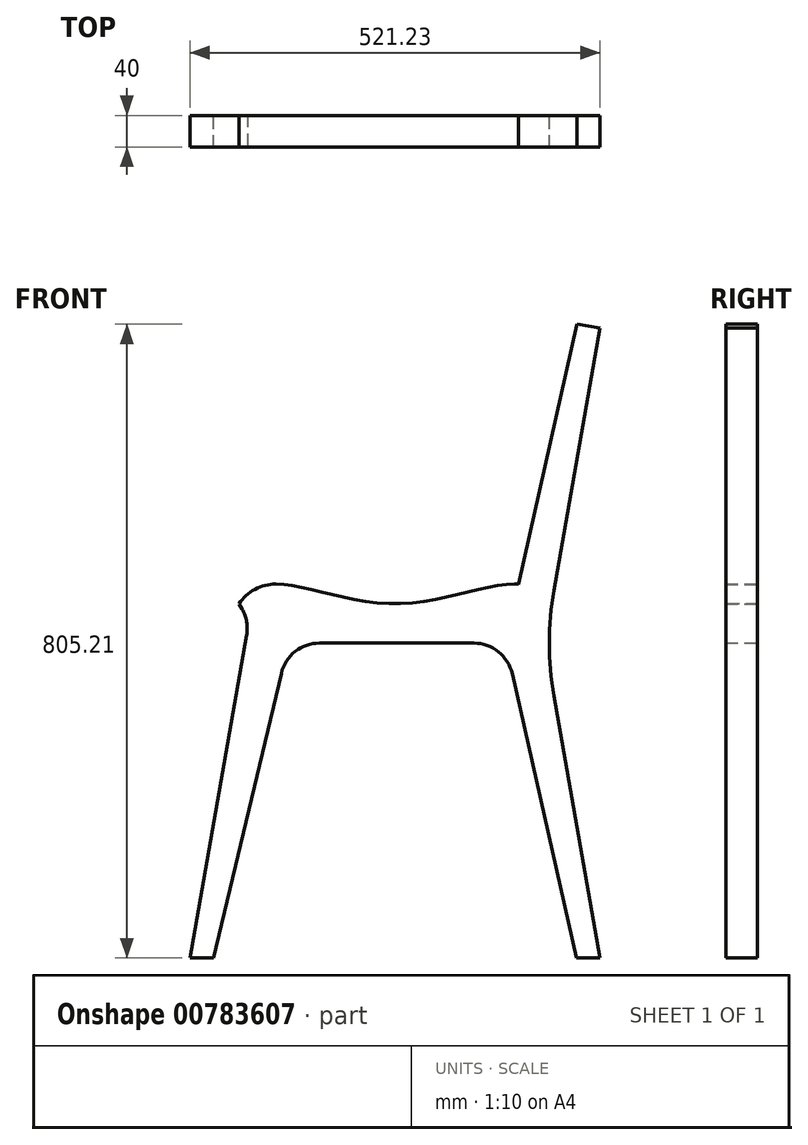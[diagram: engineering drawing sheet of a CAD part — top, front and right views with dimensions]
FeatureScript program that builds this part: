
annotation { "Feature Type Name" : "Feature", "Feature Type Description" : "" }
export const myFeature = defineFeature(function(context is Context, id is Id, definition is map)
    precondition{}
    {
        {
            var Q0;
            Q0=qCreatedBy(makeId("Front.planeOp"),FACE);
            var sketch = newSketch(context, id + "F0", { "sketchPlane" : qUnion([Q0])});
            skLineSegment(sketch, "E0.bottom", {"start": v(-200, 0) * mm, "end": v(200, 0) * mm, "construction": true});
            skLineSegment(sketch, "E0.top", {"start": v(-200, 350) * mm, "end": v(200, 350) * mm, "construction": true});
            skLineSegment(sketch, "E0.left", {"start": v(-200, 0) * mm, "end": v(-200, 350) * mm, "construction": true});
            skLineSegment(sketch, "E0.right", {"start": v(200, 0) * mm, "end": v(200, 350) * mm, "construction": true});
            skLineSegment(sketch, "E1", {"start": v(-200, 0) * mm, "end": v(-200, -450) * mm, "construction": true});
            skLineSegment(sketch, "E2", {"start": v(-200, -450) * mm, "end": v(200, -450) * mm, "construction": true});
            skLineSegment(sketch, "E3", {"start": v(200, -450) * mm, "end": v(200, 0) * mm, "construction": true});
            skLineSegment(sketch, "E4", {"start": v(261.71, 350) * mm, "end": v(232.17, 355.2) * mm});
            skLineSegment(sketch, "E5", {"start": v(261.71, 350) * mm, "end": v(203, 17.06) * mm});
            skLineSegment(sketch, "E6", {"start": v(-200, 4.9) * mm, "end": v(-178.35, 17.4) * mm});
            skCircle(sketch, "E7", {"center": v(-150, -31.7) * mm, "radius": 56.7 * mm});
            skCircle(sketch, "E8", {"center": v(153, -31.7) * mm, "radius": 56.7 * mm});
            skLineSegment(sketch, "E9", {"start": v(203, 17.06) * mm, "end": v(162.85, 24.14) * mm});
            skLineSegment(sketch, "E10", {"start": v(-200, 4.9) * mm, "end": v(-168.3, -50) * mm});
            skFitSpline(sketch, "E11", {"points": [v(-150, 25) * mm, v(0, 0) * mm, v(153, 25) * mm], "startDerivative": vector(214.7, 0) * mm, "endDerivative": vector(230.94, 0) * mm});
            skLineSegment(sketch, "E12", {"start": v(153, 25) * mm, "end": v(153, -31.7) * mm});
            skLineSegment(sketch, "E13", {"start": v(-150, 25) * mm, "end": v(-150, -31.7) * mm});
            skLineSegment(sketch, "E14", {"start": v(261.71, 350) * mm, "end": v(261.71, -450) * mm, "construction": true});
            skLineSegment(sketch, "E15", {"start": v(261.71, -450) * mm, "end": v(203, -117.06) * mm});
            skLineSegment(sketch, "E16", {"start": v(191.18, -50) * mm, "end": v(-168.3, -50) * mm});
            skLineSegment(sketch, "E17", {"start": v(-184.15, -22.55) * mm, "end": v(-259.52, -450) * mm});
            skLineSegment(sketch, "E18", {"start": v(-259.52, -450) * mm, "end": v(-229.52, -450) * mm});
            skLineSegment(sketch, "E19", {"start": v(-229.52, -450) * mm, "end": v(-134.15, -50) * mm});
            skLineSegment(sketch, "E20", {"start": v(141.18, -50) * mm, "end": v(231.71, -450) * mm});
            skLineSegment(sketch, "E21", {"start": v(231.71, -450) * mm, "end": v(261.71, -450) * mm});
            skLineSegment(sketch, "E22", {"start": v(232.17, 355.2) * mm, "end": v(141.18, -50) * mm});
            skPoint(sketch, "E23.newPointB", {"position": v(191.18, -50) * mm});
            skArc(sketch, "E23.filletArc", {"start": v(203, 17.06) * mm, "mid": v(197.14, -50) * mm, "end": v(203, -117.06) * mm});
            skSolve(sketch);
        }
        {
            var Q0;
            {var subQ5=sQuery(id+"F0.wireOp",EDGE,"E4");Q0=makeQuery(id+"F0.imprint","IMPRINT",FACE,{"disambiguationData":[TD([[makeQuery(id+"F0.imprint","IMPRINT",EDGE,{"derivedFrom":subQ5}),1.0]])]});}
            var Q1;
            {var subQ0=sQuery(id+"F0.wireOp",EDGE,"E9");Q1=makeQuery(id+"F0.imprint","IMPRINT",FACE,{"disambiguationData":[TD([[makeQuery(id+"F0.imprint","IMPRINT",EDGE,{"derivedFrom":subQ0}),1.0]])]});}
            var Q2;
            {var subQ0=sQuery(id+"F0.wireOp",EDGE,"E8");var subQ1=makeQuery(id+"F0.imprint","INTERSECT",VERTEX,{"derivedFrom":[subQ0,sQuery(id+"F0.wireOp",EDGE,"E9")]});Q2=makeQuery(id+"F0.imprint","IMPRINT",FACE,{"disambiguationData":[TD([[makeQuery(id+"F0.imprint","IMPRINT",EDGE,{"disambiguationData":[TD([[subQ1,1.0]])],"derivedFrom":subQ0}),1.0]])]});}
            var Q3;
            {var subQ1=sQuery(id+"F0.wireOp",EDGE,"E8");var subQ3=sQuery(id+"F0.wireOp",EDGE,"E16");var subQ4=makeQuery(id+"F0.imprint","INTERSECT",VERTEX,{"derivedFrom":[subQ1,subQ3]});Q3=makeQuery(id+"F0.imprint","IMPRINT",FACE,{"disambiguationData":[TD([[makeQuery(id+"F0.imprint","IMPRINT",EDGE,{"disambiguationData":[TD([[subQ4,1.0]])],"derivedFrom":subQ1}),1.0]])]});}
            var Q4;
            {var subQ1=sQuery(id+"F0.wireOp",EDGE,"E8");var subQ3=sQuery(id+"F0.wireOp",EDGE,"E22");var subQ4=makeQuery(id+"F0.imprint","INTERSECT",VERTEX,{"derivedFrom":[subQ1,subQ3]});Q4=makeQuery(id+"F0.imprint","IMPRINT",FACE,{"disambiguationData":[TD([[makeQuery(id+"F0.imprint","IMPRINT",EDGE,{"disambiguationData":[TD([[subQ4,-1.0]])],"derivedFrom":subQ3}),-1.0]])]});}
            var Q5;
            {var subQ0=sQuery(id+"F0.wireOp",EDGE,"E11");Q5=makeQuery(id+"F0.imprint","IMPRINT",FACE,{"disambiguationData":[TD([[makeQuery(id+"F0.imprint","IMPRINT",EDGE,{"derivedFrom":subQ0}),-1.0]])]});}
            var Q6;
            {var subQ3=sQuery(id+"F0.wireOp",EDGE,"E8");var subQ5=sQuery(id+"F0.wireOp",EDGE,"E20");var subQ6=makeQuery(id+"F0.imprint","INTERSECT",VERTEX,{"derivedFrom":[subQ3,subQ5]});Q6=makeQuery(id+"F0.imprint","IMPRINT",FACE,{"disambiguationData":[TD([[makeQuery(id+"F0.imprint","IMPRINT",EDGE,{"disambiguationData":[TD([[subQ6,-1.0]])],"derivedFrom":subQ3}),1.0]])]});}
            var Q7;
            {var subQ0=sQuery(id+"F0.wireOp",EDGE,"E20");var subQ1=sQuery(id+"F0.wireOp",EDGE,"E5");var subQ2=makeQuery(id+"F0.imprint","INTERSECT",VERTEX,{"derivedFrom":[subQ1,subQ0]});Q7=makeQuery(id+"F0.imprint","IMPRINT",FACE,{"disambiguationData":[TD([[makeQuery(id+"F0.imprint","IMPRINT",EDGE,{"disambiguationData":[TD([[subQ2,1.0]])],"derivedFrom":subQ1}),-1.0]])]});}
            var Q8;
            {var subQ0=sQuery(id+"F0.wireOp",EDGE,"E15");var subQ3=sQuery(id+"F0.wireOp",EDGE,"E8");var subQ5=makeQuery(id+"F0.imprint","INTERSECT",VERTEX,{"derivedFrom":[subQ3,subQ0]});Q8=makeQuery(id+"F0.imprint","IMPRINT",FACE,{"disambiguationData":[TD([[makeQuery(id+"F0.imprint","IMPRINT",EDGE,{"disambiguationData":[TD([[subQ5,1.0]])],"derivedFrom":subQ3}),1.0]])]});}
            var Q9;
            {var subQ0=sQuery(id+"F0.wireOp",EDGE,"E21");Q9=makeQuery(id+"F0.imprint","IMPRINT",FACE,{"disambiguationData":[TD([[makeQuery(id+"F0.imprint","IMPRINT",EDGE,{"derivedFrom":subQ0}),1.0]])]});}
            var Q10;
            {var subQ3=sQuery(id+"F0.wireOp",EDGE,"E7");var subQ7=makeQuery(id+"F0.imprint","INTERSECT",VERTEX,{"derivedFrom":[sQuery(id+"F0.wireOp",EDGE,"E6"),subQ3]});Q10=makeQuery(id+"F0.imprint","IMPRINT",FACE,{"disambiguationData":[TD([[makeQuery(id+"F0.imprint","IMPRINT",EDGE,{"disambiguationData":[TD([[subQ7,1.0]])],"derivedFrom":subQ3}),1.0]])]});}
            var Q11;
            {var subQ0=sQuery(id+"F0.wireOp",EDGE,"E17");var subQ1=sQuery(id+"F0.wireOp",EDGE,"E7");var subQ2=makeQuery(id+"F0.imprint","INTERSECT",VERTEX,{"derivedFrom":[subQ1,subQ0]});Q11=makeQuery(id+"F0.imprint","IMPRINT",FACE,{"disambiguationData":[TD([[makeQuery(id+"F0.imprint","IMPRINT",EDGE,{"disambiguationData":[TD([[subQ2,-1.0]])],"derivedFrom":subQ1}),1.0]])]});}
            var Q12;
            {var subQ5=sQuery(id+"F0.wireOp",EDGE,"E18");Q12=makeQuery(id+"F0.imprint","IMPRINT",FACE,{"disambiguationData":[TD([[makeQuery(id+"F0.imprint","IMPRINT",EDGE,{"derivedFrom":subQ5}),1.0]])]});}
            extrude(context, id + "F1", {"entities" : qUnion([Q0, Q1, Q2, Q3, Q4, Q5, Q6, Q7, Q8, Q9, Q10, Q11, Q12]), "depth" : 40 * mm, "offsetDistance" : 25 * mm});
        }
        {
            var Q0;
            Q0=makeQuery(id+"F1.opExtrude","SWEPT_EDGE",EDGE,{"disambiguationData":[OSD([sQuery(id+"F0.wireOp",EDGE,"E10"),sQuery(id+"F0.wireOp",EDGE,"E16"),sQuery(id+"F0.wireOp",EDGE,"E17")])]});
            fillet(context, id + "F2", {"entities" : qUnion([Q0]), "radius" : 50 * mm, "tangentPropagation" : true, "allowEdgeOverflow" : false});
        }
        {
            var Q0;
            Q0=makeQuery(id+"F1.opExtrude","SWEPT_EDGE",EDGE,{"disambiguationData":[OSD([sQuery(id+"F0.wireOp",EDGE,"E16"),sQuery(id+"F0.wireOp",EDGE,"E19")])]});
            fillet(context, id + "F3", {"entities" : qUnion([Q0]), "radius" : 50 * mm, "tangentPropagation" : true, "allowEdgeOverflow" : false});
        }
        {
            var Q0;
            Q0=makeQuery(id+"F1.opExtrude","SWEPT_EDGE",EDGE,{"disambiguationData":[OSD([sQuery(id+"F0.wireOp",EDGE,"E16"),sQuery(id+"F0.wireOp",EDGE,"E20"),sQuery(id+"F0.wireOp",EDGE,"E22")])]});
            fillet(context, id + "F4", {"entities" : qUnion([Q0]), "radius" : 50 * mm, "tangentPropagation" : true, "allowEdgeOverflow" : false});
        }
    });
